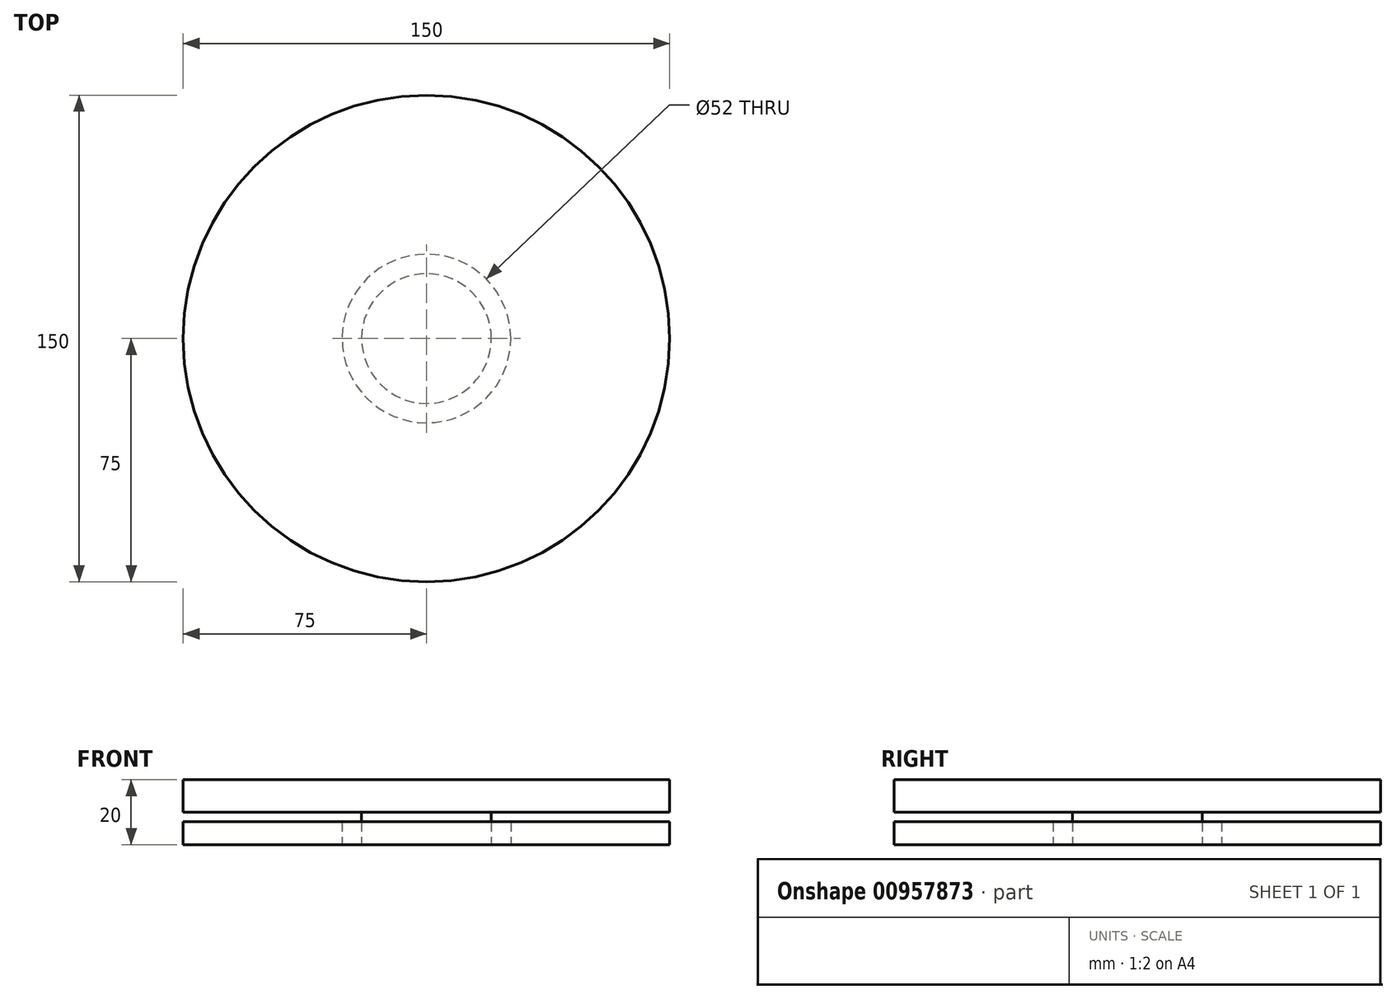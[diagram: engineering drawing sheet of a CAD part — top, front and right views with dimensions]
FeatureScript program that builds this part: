
annotation { "Feature Type Name" : "Feature", "Feature Type Description" : "" }
export const myFeature = defineFeature(function(context is Context, id is Id, definition is map)
    precondition{}
    {
        {
            var Q0;
            Q0=qCreatedBy(makeId("Top.planeOp"),FACE);
            var sketch = newSketch(context, id + "F0", { "sketchPlane" : qUnion([Q0])});
            skCircle(sketch, "E0", {"center": v(0, 0) * mm, "radius": 75 * mm});
            skCircle(sketch, "E1", {"center": v(0, 0) * mm, "radius": 26 * mm});
            skSolve(sketch);
        }
        {
            var Q0;
            Q0=makeQuery(id+"F0.imprint","IMPRINT",FACE,{"disambiguationData":[TD([[makeQuery(id+"F0.imprint","IMPRINT",EDGE,{"derivedFrom":sQuery(id+"F0.wireOp",EDGE,"E0")}),1.0]])]});
            extrude(context, id + "F1", {"entities" : qUnion([Q0]), "depth" : 7 * mm, "offsetDistance" : 25 * mm});
        }
        {
            var Q0;
            Q0=qCreatedBy(makeId("Top.planeOp"),FACE);
            var sketch = newSketch(context, id + "F2", { "sketchPlane" : qUnion([Q0])});
            skCircle(sketch, "E2", {"center": v(0, 0) * mm, "radius": 20 * mm});
            skSolve(sketch);
        }
        {
            var Q0;
            Q0=makeQuery(id+"F2.imprint","IMPRINT",FACE,{"disambiguationData":[TD([[makeQuery(id+"F2.imprint","IMPRINT",EDGE,{"derivedFrom":sQuery(id+"F2.wireOp",EDGE,"E2")}),1.0]])]});
            extrude(context, id + "F3", {"entities" : qUnion([Q0]), "depth" : 10 * mm, "offsetDistance" : 25 * mm});
        }
        {
            var Q0;
            Q0=makeQuery(id+"F3.opExtrude","CAP_FACE",FACE,{"disambiguationData":[OSD([sQuery(id+"F2.wireOp",EDGE,"E2")])],"isStart":false});
            var sketch = newSketch(context, id + "F4", { "sketchPlane" : qUnion([Q0])});
            skCircle(sketch, "E3", {"center": v(0, 0) * mm, "radius": 75 * mm});
            skSolve(sketch);
        }
        {
            var Q0;
            Q0=makeQuery(id+"F4.imprint","IMPRINT",FACE,{"disambiguationData":[TD([[makeQuery(id+"F4.imprint","IMPRINT",EDGE,{"derivedFrom":sQuery(id+"F4.wireOp",EDGE,"E3")}),1.0]])]});
            var Q1;
            Q1=makeQuery(id+"F4.imprint","IMPRINT",FACE,{"disambiguationData":[TD([[makeQuery(id+"F4.imprint","IMPRINT",EDGE,{"derivedFrom":makeQuery(id+"F3.opExtrude","CAP_EDGE",EDGE,{"disambiguationData":[OSD([sQuery(id+"F2.wireOp",EDGE,"E2")])],"isStart":false})}),1.0]])]});
            extrude(context, id + "F5", {"entities" : qUnion([Q0, Q1]), "operationType" : NewBodyOperationType.ADD, "depth" : 10 * mm, "offsetDistance" : 25 * mm});
        }
    });
